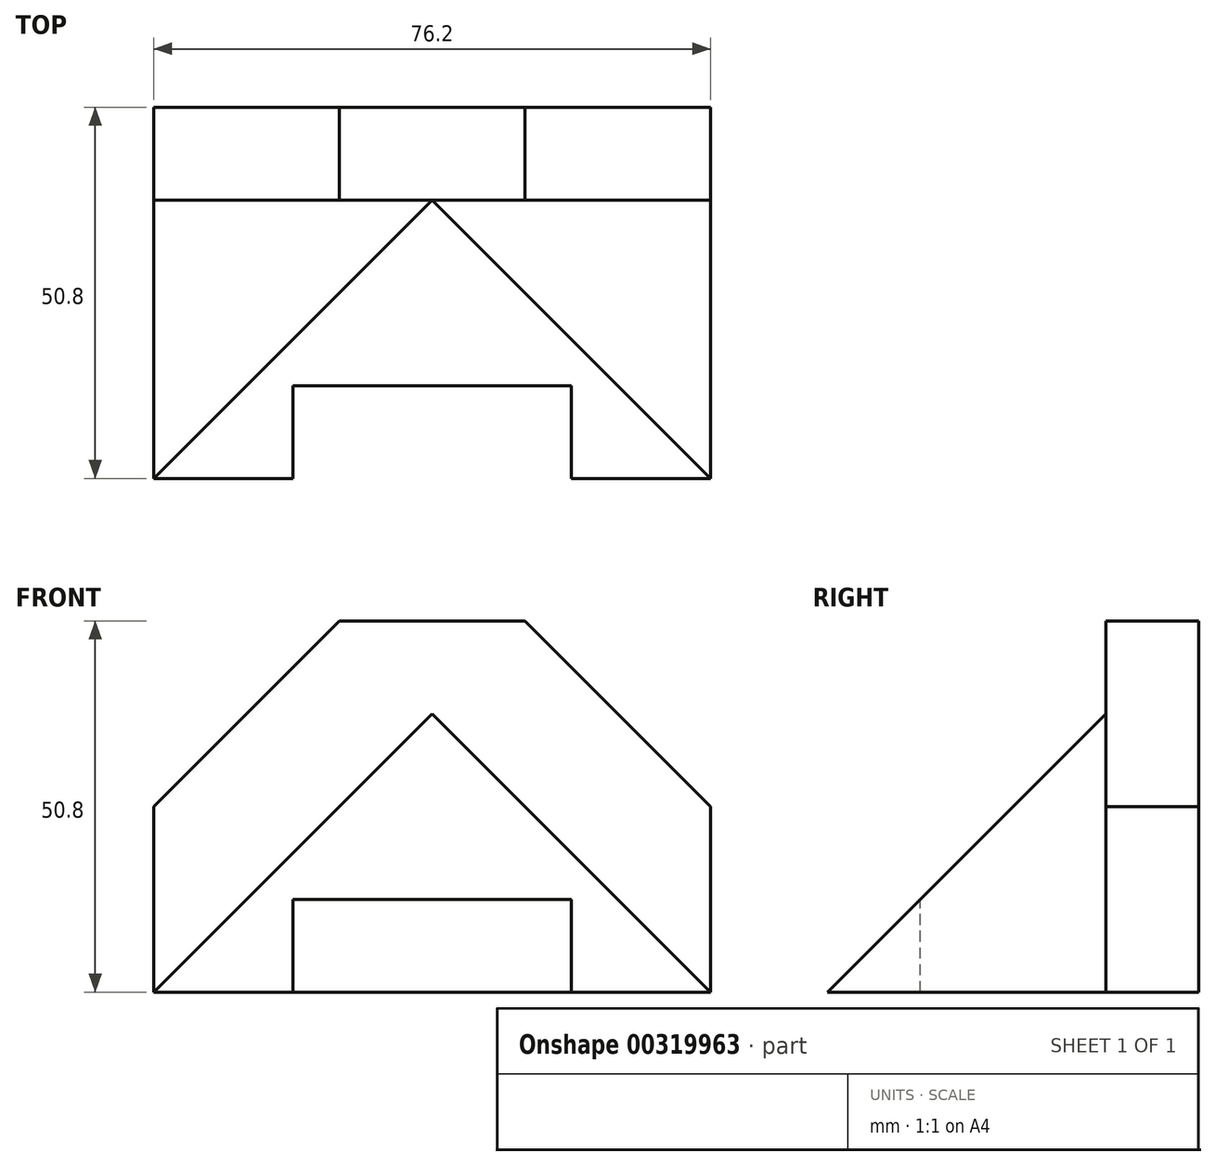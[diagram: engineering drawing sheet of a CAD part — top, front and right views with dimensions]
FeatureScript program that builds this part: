
annotation { "Feature Type Name" : "Feature", "Feature Type Description" : "" }
export const myFeature = defineFeature(function(context is Context, id is Id, definition is map)
    precondition{}
    {
        {
            var Q0;
            Q0=qCreatedBy(makeId("Front.planeOp"),FACE);
            var sketch = newSketch(context, id + "F0", { "sketchPlane" : qUnion([Q0])});
            skLineSegment(sketch, "E0", {"start": v(-38.1, 0) * mm, "end": v(38.1, 0) * mm});
            skLineSegment(sketch, "E1", {"start": v(38.1, 0) * mm, "end": v(38.1, 25.4) * mm});
            skLineSegment(sketch, "E2", {"start": v(38.1, 25.4) * mm, "end": v(12.7, 50.8) * mm});
            skLineSegment(sketch, "E3", {"start": v(12.7, 50.8) * mm, "end": v(-12.7, 50.8) * mm});
            skLineSegment(sketch, "E4", {"start": v(-12.7, 50.8) * mm, "end": v(-38.1, 25.4) * mm});
            skLineSegment(sketch, "E5", {"start": v(-38.1, 25.4) * mm, "end": v(-38.1, 0) * mm});
            skSolve(sketch);
        }
        {
            var Q0;
            Q0 = qSketchRegion(id + "F0", true);
            extrude(context, id + "F1", {"entities" : qUnion([Q0]), "oppositeDirection" : true, "depth" : 12.7 * mm});
        }
        {
            var Q0;
            Q0=makeQuery(id+"F1.opExtrude","CAP_FACE",FACE,{"disambiguationData":[OSD([sQuery(id+"F0.wireOp",EDGE,"E0"),sQuery(id+"F0.wireOp",EDGE,"E1"),sQuery(id+"F0.wireOp",EDGE,"E2"),sQuery(id+"F0.wireOp",EDGE,"E3"),sQuery(id+"F0.wireOp",EDGE,"E4"),sQuery(id+"F0.wireOp",EDGE,"E5")])],"isStart":true});
            var sketch = newSketch(context, id + "F2", { "sketchPlane" : qUnion([Q0])});
            skLineSegment(sketch, "E6", {"start": v(-38.1, 0) * mm, "end": v(0, 38.1) * mm});
            skLineSegment(sketch, "E7", {"start": v(0, 38.1) * mm, "end": v(38.1, 0) * mm});
            skLineSegment(sketch, "E8", {"start": v(38.1, 0) * mm, "end": v(-38.1, 0) * mm});
            skSolve(sketch);
        }
        {
            var Q0;
            Q0=makeQuery(id+"F2.imprint","IMPRINT",FACE,{"disambiguationData":[TD([[makeQuery(id+"F2.imprint","IMPRINT",EDGE,{"derivedFrom":sQuery(id+"F2.wireOp",EDGE,"E6")}),-1.0]])]});
            extrude(context, id + "F3", {"entities" : qUnion([Q0]), "operationType" : NewBodyOperationType.ADD, "depth" : 38.1 * mm});
        }
        {
            var Q0;
            Q0=makeQuery(id+"F1.opExtrude","SWEPT_FACE",FACE,{"disambiguationData":[OSD([sQuery(id+"F0.wireOp",EDGE,"E1")])]});
            var sketch = newSketch(context, id + "F4", { "sketchPlane" : qUnion([Q0])});
            skLineSegment(sketch, "E9", {"start": v(-38.1, 0) * mm, "end": v(0, 38.1) * mm});
            skLineSegment(sketch, "E10", {"start": v(0, 38.1) * mm, "end": v(-38.1, 38.1) * mm});
            skLineSegment(sketch, "E11", {"start": v(-38.1, 38.1) * mm, "end": v(-38.1, 0) * mm});
            skSolve(sketch);
        }
        {
            var Q0;
            Q0=makeQuery(id+"F4.imprint","IMPRINT",FACE,{"disambiguationData":[TD([[makeQuery(id+"F4.imprint","IMPRINT",EDGE,{"derivedFrom":sQuery(id+"F4.wireOp",EDGE,"E9")}),1.0]])]});
            extrude(context, id + "F5", {"entities" : qUnion([Q0]), "operationType" : NewBodyOperationType.REMOVE, "oppositeDirection" : true, "depth" : 97.54 * mm});
        }
        {
            var Q0;
            Q0=makeQuery(id+"F1.opExtrude","SWEPT_FACE",FACE,{"disambiguationData":[OSD([sQuery(id+"F0.wireOp",EDGE,"E3")])]});
            var sketch = newSketch(context, id + "F6", { "sketchPlane" : qUnion([Q0])});
            skLineSegment(sketch, "E12.bottom", {"start": v(-19.05, -25.4) * mm, "end": v(19.05, -25.4) * mm});
            skLineSegment(sketch, "E12.top", {"start": v(-19.05, -38.1) * mm, "end": v(19.05, -38.1) * mm});
            skLineSegment(sketch, "E12.left", {"start": v(-19.05, -25.4) * mm, "end": v(-19.05, -38.1) * mm});
            skLineSegment(sketch, "E12.right", {"start": v(19.05, -25.4) * mm, "end": v(19.05, -38.1) * mm});
            skSolve(sketch);
        }
        {
            var Q0;
            Q0 = qSketchRegion(id + "F6", true);
            extrude(context, id + "F7", {"entities" : qUnion([Q0]), "operationType" : NewBodyOperationType.REMOVE, "endBound" : BoundingType.THROUGH_ALL, "oppositeDirection" : true, "depth" : 25.4 * mm});
        }
    });
